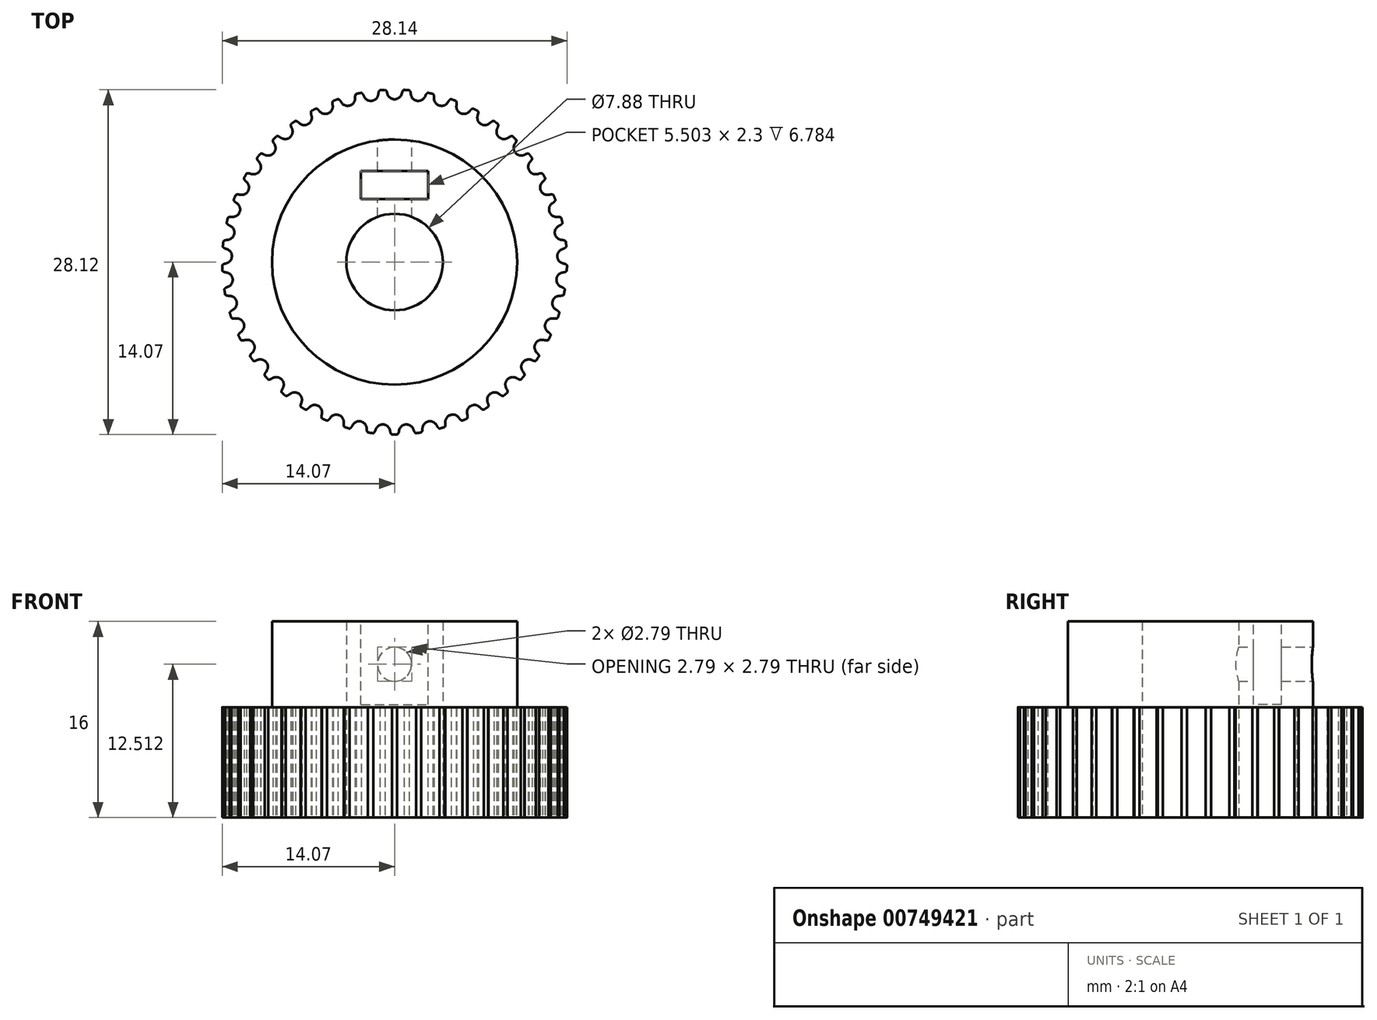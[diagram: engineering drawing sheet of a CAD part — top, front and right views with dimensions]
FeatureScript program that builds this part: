
annotation { "Feature Type Name" : "Feature", "Feature Type Description" : "" }
export const myFeature = defineFeature(function(context is Context, id is Id, definition is map)
    precondition{}
    {
        {
            assignVariable(context, id + "F0", {"name" : "Teeth", "anyValue" : 45});
        }
        {
            var Q0;
            Q0=qCreatedBy(makeId("Top.planeOp"),FACE);
            var sketch = newSketch(context, id + "F1", { "sketchPlane" : qUnion([Q0])});
            skCircle(sketch, "E0", {"center": v(0, 0) * mm, "radius": 14.07 * mm});
            skSolve(sketch);
        }
        {
            var Q0;
            Q0=qCreatedBy(makeId("Top.planeOp"),FACE);
            var sketch = newSketch(context, id + "F2", { "sketchPlane" : qUnion([Q0])});
            skArc(sketch, "E1.0", {"start": v(0.77, 14.05) * mm, "mid": v(0, 14.07) * mm, "end": v(-0.77, 14.05) * mm});
            skLineSegment(sketch, "E2", {"start": v(0, 0) * mm, "end": v(0, 13.9) * mm, "construction": true});
            skArc(sketch, "E3", {"start": v(0, 13.28) * mm, "mid": v(-0.38, 13.42) * mm, "end": v(-0.6, 13.76) * mm});
            skArc(sketch, "E4", {"start": v(-0.6, 13.76) * mm, "mid": v(-0.63, 13.87) * mm, "end": v(-0.68, 13.96) * mm});
            skArc(sketch, "E5", {"start": v(-0.68, 13.96) * mm, "mid": v(-0.71, 14.01) * mm, "end": v(-0.77, 14.05) * mm});
            skArc(sketch, "E6.MirrorCS", {"start": v(0, 13.28) * mm, "mid": v(0.38, 13.42) * mm, "end": v(0.6, 13.76) * mm});
            skArc(sketch, "E7.MirrorCS", {"start": v(0.68, 13.96) * mm, "mid": v(0.71, 14.01) * mm, "end": v(0.77, 14.05) * mm});
            skArc(sketch, "E8.MirrorCS", {"start": v(0.6, 13.76) * mm, "mid": v(0.63, 13.87) * mm, "end": v(0.68, 13.96) * mm});
            skSolve(sketch);
        }
        {
            var Q0;
            Q0=qSketchRegion(id+"F1",true);
            extrude(context, id + "F3", {"entities" : qUnion([Q0]), "depth" : 9 * mm, "offsetDistance" : 25 * mm});
        }
        {
            var Q0;
            Q0=makeQuery(id+"F2.imprint","IMPRINT",FACE,{"disambiguationData":[TD([[makeQuery(id+"F2.imprint","IMPRINT",EDGE,{"derivedFrom":sQuery(id+"F2.wireOp",EDGE,"E1.0")}),1.0]])]});
            extrude(context, id + "F4", {"entities" : qUnion([Q0]), "depth" : 25 * mm, "offsetDistance" : 25 * mm});
        }
        {
            var Q0;
            Q0=makeQuery(id+"F4.opExtrude","SWEPT_BODY",BODY,{"disambiguationData":[OSD([sQuery(id+"F2.wireOp",EDGE,"E1.0"),sQuery(id+"F2.wireOp",EDGE,"E3"),sQuery(id+"F2.wireOp",EDGE,"E4"),sQuery(id+"F2.wireOp",EDGE,"E5"),sQuery(id+"F2.wireOp",EDGE,"E6.MirrorCS"),sQuery(id+"F2.wireOp",EDGE,"E7.MirrorCS"),sQuery(id+"F2.wireOp",EDGE,"E8.MirrorCS")])]});
            var Q1;
            Q1=sQuery(id+"F1.wireOp",EDGE,"E0");
            circularPattern(context, id + "F5", {"operationType" : NewBodyOperationType.REMOVE, "entities" : qUnion([Q0]), "axis" : qUnion([Q1]), "angle" : 360 * degree, "instanceCount" : getVariable(context, 'Teeth'), "equalSpace" : true});
        }
        {
            var Q0;
            Q0=makeQuery(id+"F3.opExtrude","CAP_FACE",FACE,{"disambiguationData":[OSD([sQuery(id+"F1.wireOp",EDGE,"E0")])],"isStart":false});
            var sketch = newSketch(context, id + "F6", { "sketchPlane" : qUnion([Q0])});
            skCircle(sketch, "E9", {"center": v(0, 0) * mm, "radius": 10 * mm});
            skSolve(sketch);
        }
        {
            var Q0;
            Q0=qSketchRegion(id+"F6",true);
            extrude(context, id + "F7", {"entities" : qUnion([Q0]), "operationType" : NewBodyOperationType.ADD, "depth" : 7 * mm, "offsetDistance" : 25 * mm});
        }
        {
            var Q0;
            Q0=qCreatedBy(makeId("Top.planeOp"),FACE);
            var sketch = newSketch(context, id + "F8", { "sketchPlane" : qUnion([Q0])});
            skCircle(sketch, "E10", {"center": v(0, 0) * mm, "radius": 3.94 * mm});
            skSolve(sketch);
        }
        {
            var Q0;
            Q0=qSketchRegion(id+"F8",true);
            var Q1;
            Q1=sQuery(id+"F8.wireOp",EDGE,"E10");
            extrude(context, id + "F9", {"entities" : qUnion([Q0]), "operationType" : NewBodyOperationType.REMOVE, "surfaceEntities" : qUnion([Q1]), "endBound" : BoundingType.THROUGH_ALL, "depth" : 25 * mm, "offsetDistance" : 25 * mm});
        }
        {
            var Q0;
            Q0=makeQuery(id+"F7.opExtrude","CAP_FACE",FACE,{"disambiguationData":[OSD([sQuery(id+"F6.wireOp",EDGE,"E9")])],"isStart":false});
            var sketch = newSketch(context, id + "F10", { "sketchPlane" : qUnion([Q0])});
            skLineSegment(sketch, "E11", {"start": v(0, 10) * mm, "end": v(0, 7.44) * mm, "construction": true});
            skLineSegment(sketch, "E12.bottom", {"start": v(-2.75, 7.44) * mm, "end": v(2.75, 7.44) * mm});
            skLineSegment(sketch, "E12.top", {"start": v(-2.75, 7.44) * mm, "end": v(2.75, 7.44) * mm});
            skLineSegment(sketch, "E12.left", {"start": v(-2.75, 7.44) * mm, "end": v(-2.75, 7.44) * mm});
            skLineSegment(sketch, "E12.right", {"start": v(2.75, 7.44) * mm, "end": v(2.75, 7.44) * mm});
            skPoint(sketch, "E12.middle", {"position": v(0, 7.44) * mm});
            skLineSegment(sketch, "E13.top", {"start": v(-2.75, 5.14) * mm, "end": v(2.75, 5.14) * mm});
            skLineSegment(sketch, "E13.left", {"start": v(-2.75, 7.44) * mm, "end": v(-2.75, 5.14) * mm});
            skLineSegment(sketch, "E13.right", {"start": v(2.75, 7.44) * mm, "end": v(2.75, 5.14) * mm});
            skSolve(sketch);
        }
        {
            var Q0;
            Q0=qSketchRegion(id+"F10",true);
            extrude(context, id + "F11", {"entities" : qUnion([Q0]), "operationType" : NewBodyOperationType.REMOVE, "oppositeDirection" : true, "depth" : 6.78 * mm, "offsetDistance" : 25 * mm});
        }
        {
            var Q0;
            Q0=makeQuery(id+"F11.boolean.opBoolean","COPY",FACE,{"derivedFrom":makeQuery(id+"F11.opExtrude","SWEPT_FACE",FACE,{"disambiguationData":[OSD([sQuery(id+"F10.wireOp",EDGE,"E13.top")])]})});
            var sketch = newSketch(context, id + "F12", { "sketchPlane" : qUnion([Q0])});
            skLineSegment(sketch, "E14", {"start": v(0, 16) * mm, "end": v(0, 13.9) * mm, "construction": true});
            skLineSegment(sketch, "E15", {"start": v(0, 13.9) * mm, "end": v(0, 11.12) * mm, "construction": true});
            skCircle(sketch, "E16", {"center": v(0, 12.51) * mm, "radius": 1.4 * mm});
            skSolve(sketch);
        }
        {
            var Q0;
            Q0=makeQuery(id+"F12.imprint","IMPRINT",FACE,{"disambiguationData":[TD([[makeQuery(id+"F12.imprint","IMPRINT",EDGE,{"derivedFrom":sQuery(id+"F12.wireOp",EDGE,"E16")}),1.0]])]});
            extrude(context, id + "F13", {"entities" : qUnion([Q0]), "operationType" : NewBodyOperationType.REMOVE, "oppositeDirection" : true, "depth" : 5 * mm, "offsetDistance" : 25 * mm, "hasSecondDirection" : true, "secondDirectionOppositeDirection" : false, "secondDirectionDepth" : 15 * mm});
        }
    });
